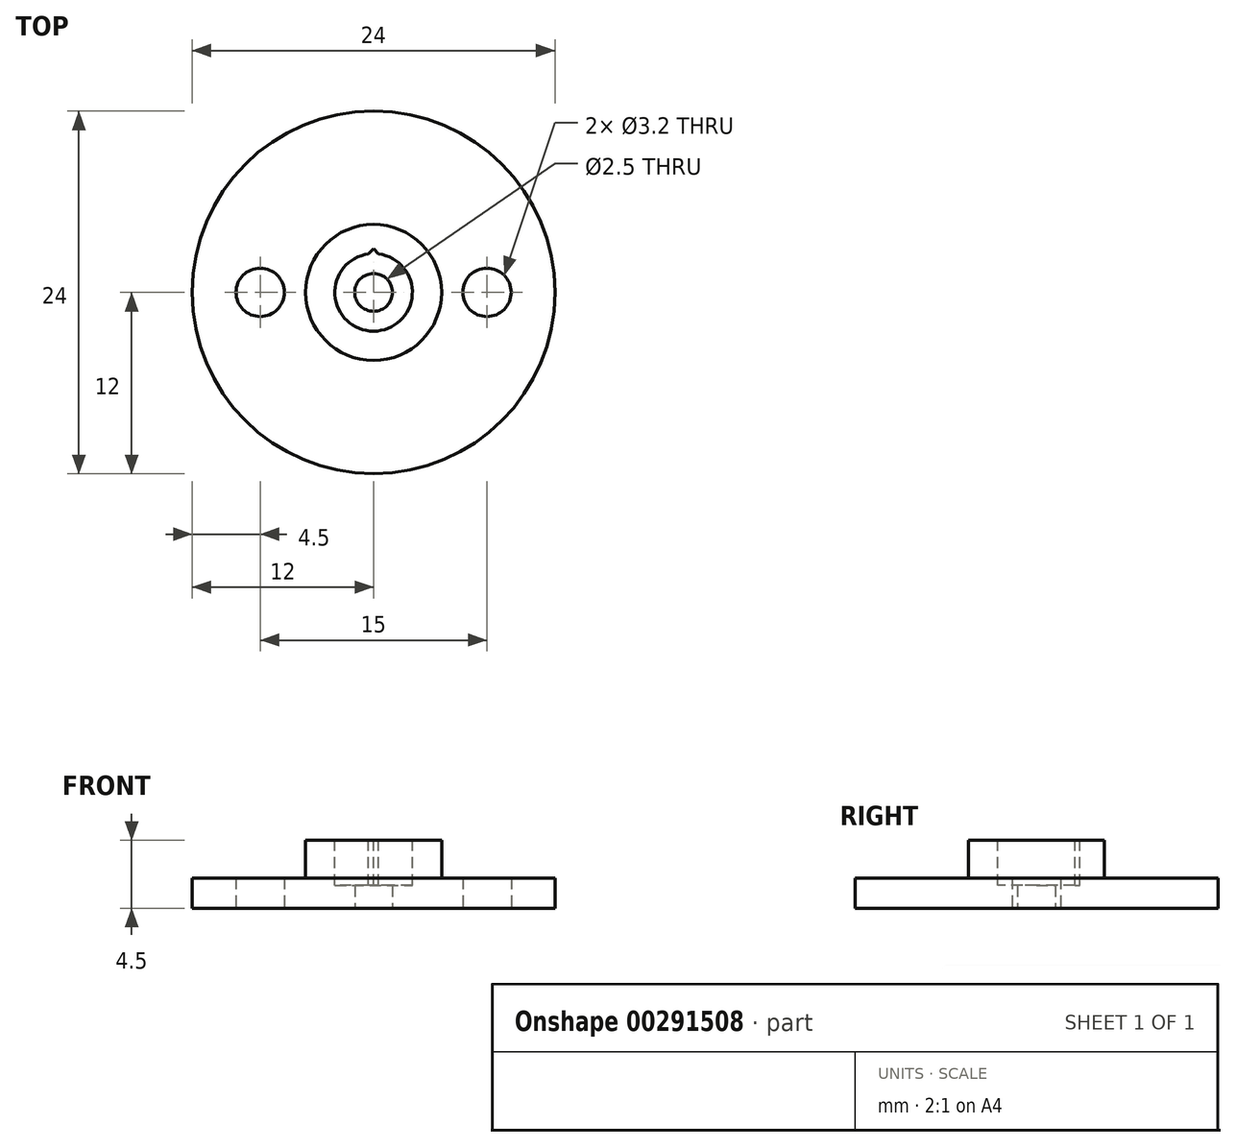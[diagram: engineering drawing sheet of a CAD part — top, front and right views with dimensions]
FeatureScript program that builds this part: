
annotation { "Feature Type Name" : "Feature", "Feature Type Description" : "" }
export const myFeature = defineFeature(function(context is Context, id is Id, definition is map)
    precondition{}
    {
        {
            var Q0;
            Q0=qCreatedBy(makeId("Top.planeOp"),FACE);
            var sketch = newSketch(context, id + "F0", { "sketchPlane" : qUnion([Q0])});
            skCircle(sketch, "E0", {"center": v(0, 0) * mm, "radius": 12 * mm});
            skSolve(sketch);
        }
        {
            var Q0;
            Q0 = qSketchRegion(id + "F0", true);
            extrude(context, id + "F1", {"entities" : qUnion([Q0]), "depth" : 2 * mm});
        }
        {
            var Q0;
            Q0=makeQuery(id+"F1.opExtrude","CAP_FACE",FACE,{"disambiguationData":[OSD([sQuery(id+"F0.wireOp",EDGE,"E0")])],"isStart":false});
            var sketch = newSketch(context, id + "F2", { "sketchPlane" : qUnion([Q0])});
            skCircle(sketch, "E1", {"center": v(0, 0) * mm, "radius": 4.5 * mm});
            skSolve(sketch);
        }
        {
            var Q0;
            Q0 = qSketchRegion(id + "F2", true);
            extrude(context, id + "F3", {"entities" : qUnion([Q0]), "operationType" : NewBodyOperationType.ADD, "depth" : 2.5 * mm});
        }
        {
            var Q0;
            Q0=makeQuery(id+"F3.opExtrude","CAP_FACE",FACE,{"disambiguationData":[OSD([sQuery(id+"F2.wireOp",EDGE,"E1")])],"isStart":false});
            var sketch = newSketch(context, id + "F4", { "sketchPlane" : qUnion([Q0])});
            skCircle(sketch, "E2", {"center": v(0, 0) * mm, "radius": 2.56 * mm});
            skSolve(sketch);
        }
        {
            var Q0;
            Q0 = qSketchRegion(id + "F4", true);
            extrude(context, id + "F5", {"entities" : qUnion([Q0]), "operationType" : NewBodyOperationType.REMOVE, "oppositeDirection" : true, "depth" : 3 * mm});
        }
        {
            var Q0;
            Q0=makeQuery(id+"F3.opExtrude","CAP_FACE",FACE,{"disambiguationData":[OSD([sQuery(id+"F2.wireOp",EDGE,"E1")])],"isStart":false});
            var sketch = newSketch(context, id + "F6", { "sketchPlane" : qUnion([Q0])});
            skLineSegment(sketch, "E3", {"start": v(-0.33, 2.54) * mm, "end": v(0, 2.88) * mm});
            skLineSegment(sketch, "E4", {"start": v(0, 2.88) * mm, "end": v(0.33, 2.54) * mm});
            skLineSegment(sketch, "E5", {"start": v(0, 0) * mm, "end": v(0, 6.38) * mm, "construction": true});
            skLineSegment(sketch, "E6", {"start": v(-0.33, 2.54) * mm, "end": v(0, 0) * mm, "construction": true});
            skLineSegment(sketch, "E7", {"start": v(0, 0) * mm, "end": v(0.33, 2.54) * mm, "construction": true});
            skArc(sketch, "E8.0", {"start": v(0.33, 2.54) * mm, "mid": v(0, 2.56) * mm, "end": v(-0.33, 2.54) * mm});
            skSolve(sketch);
        }
        {
            var Q0;
            Q0 = qSketchRegion(id + "F6", true);
            var Q1;
            Q1=makeQuery(id+"F5.boolean.opBoolean","COPY",FACE,{"derivedFrom":makeQuery(id+"F5.opExtrude","CAP_FACE",FACE,{"disambiguationData":[OSD([sQuery(id+"F4.wireOp",EDGE,"E2")])],"isStart":false})});
            extrude(context, id + "F7", {"entities" : qUnion([Q0]), "operationType" : NewBodyOperationType.REMOVE, "endBound" : BoundingType.UP_TO_SURFACE, "oppositeDirection" : true, "endBoundEntityFace" : qUnion([Q1]), "depth" : 25 * mm});
        }
        {
            var Q0;
            Q0=makeQuery(id+"F1.opExtrude","CAP_FACE",FACE,{"disambiguationData":[OSD([sQuery(id+"F0.wireOp",EDGE,"E0")])],"isStart":true});
            var sketch = newSketch(context, id + "F8", { "sketchPlane" : qUnion([Q0])});
            skCircle(sketch, "E9", {"center": v(0, 0) * mm, "radius": 1.25 * mm});
            skSolve(sketch);
        }
        {
            var Q0;
            Q0 = qSketchRegion(id + "F8", true);
            extrude(context, id + "F9", {"entities" : qUnion([Q0]), "operationType" : NewBodyOperationType.REMOVE, "endBound" : BoundingType.THROUGH_ALL, "oppositeDirection" : true, "depth" : 25 * mm});
        }
        {
            var Q0;
            Q0=makeQuery(id+"F1.opExtrude","CAP_FACE",FACE,{"disambiguationData":[OSD([sQuery(id+"F0.wireOp",EDGE,"E0")])],"isStart":true});
            var sketch = newSketch(context, id + "F10", { "sketchPlane" : qUnion([Q0])});
            skCircle(sketch, "E10", {"center": v(-7.5, 0) * mm, "radius": 1.6 * mm});
            skCircle(sketch, "E11", {"center": v(7.5, 0) * mm, "radius": 1.6 * mm});
            skSolve(sketch);
        }
        {
            var Q0;
            Q0 = qSketchRegion(id + "F10", true);
            extrude(context, id + "F11", {"entities" : qUnion([Q0]), "operationType" : NewBodyOperationType.REMOVE, "endBound" : BoundingType.UP_TO_NEXT, "oppositeDirection" : true, "depth" : 25 * mm});
        }
    });
